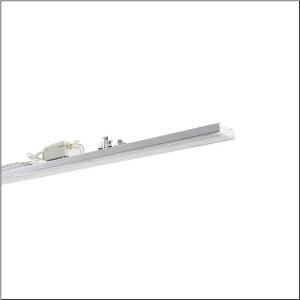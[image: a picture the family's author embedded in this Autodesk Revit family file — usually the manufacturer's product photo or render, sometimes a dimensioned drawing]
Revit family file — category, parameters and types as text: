
# Revit family: licross_21_recessed_mo_52te12dn465g
name_source: partatom
category: Lighting Fixtures
units: mm (PartAtom-declared; Revit-internal decimal feet)

## family parameters
Cut with Voids When Loaded = No
Host = Face
Light Source = No
Part Type = Normal
Room Calculation Point = No
Round Connector Dimension = Use Diameter
Shared = No

## types (1)
- --- (1 x LED, 6590 lm, 36.3 W, 4000K)
    Apparent Load = 36 VA
    CIE Flux Codes = 72 92 99 100 100
    Color Rendering = 80
    Color Temperature = 4000K
    Default Elevation = 1800 mm
    Description = Licross 21 Recessed MO, luminaire insert, of sheet steel, galvanised, coil coated, white, length: 1.500mm, width: 66mm, height: 67mm, LED rated luminous flux: 6.590lm, light colour: 840, SDCM (Standard Deviation of Colour Matching)MacAdam ≤ 3 SDCM (initial), control gear: DALI 2, with plug, 5-pole, with phase selection, mains connection: 220..240V, AC, 50/60Hz, rated input power: 36W, internal wiring halogen-free, primary optical cover: cover, of PMMA, light emission: direct distribution, primary light characteristic: symmetric, protection rating (complete): IP54, insulation class (complete): insulation class I (protective earthing), certification: CE, ENEC, VDE, UKCA, protection symbol: D if used in an environment with non-conductive dust loads with corresponding accessories, impact resistance: IK06, permissible ambient temperature for indoor applications: -25..+40°C, corresponds to IFS (International Featured Standards) requirements for safety and quality in the food industry, reducing of maximum allowable ambient temperature of 5°C with ceiling mounting, LABS conformity tested according to VDMA 24364:2018-05, The light source and the operating device comply with the requirements of the Ecodesign Regulation (EU) 2019/2020 and are replaceable in accordance with this regulation, packaging unit: 1 piece
    Height = 58 mm
    Lamp = 1 x LED
    Lamp Light Flux = 6590 lm
    Lamp Power = 36.3 W
    Lamp count = 1
    Length = 1500 mm
    Luminous efficacy = 182 lm/W
    Manufacturer = Siteco
    ModVariant = No
    Model = 52TE12DN465G
    Mounting Place = Ceiling
    Mounting Type = Pendant
    Number of Poles = 1
    OnlyDefault = Yes
    Power Factor = 1
    Product Name = Licross 21 Recessed MO
    Product group = luminaire insert | ceiling pendant
    ProductGroupID = 901
    Protection Class = Protection class I
    Protection Degree = IP 54
    RLX_Detail_Level = 1
    RLX_Emergency_Light_Flux = 0 lm
    RLX_Emergency_Type = 0
    RLX_Emergency_Type_DB = No
    RlxData = <blob elided: 24789 chars, md5=79360dbc>
    Socket = socket
    Standby Power = 0 W
    System Light Flux = 6590 lm
    System Power = 36 W
    Type Comments = factory setting: luminous flux: 100 % | dim-lin: 254 | 242 mA
    Type Image = l_1296930.jpg
    URL = http://relux.com
    VarID = @adj_088267
    Voltage = 0 V
    Weight = 0.00 kg
    Width = 66 mm

## geometry (parser evidence)
native form markers: Blend x4, Sweep x11
no freeform markers — native parametric forms only
